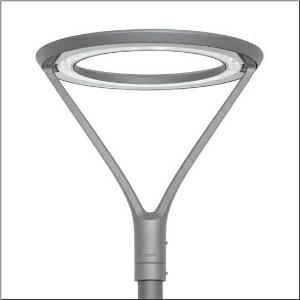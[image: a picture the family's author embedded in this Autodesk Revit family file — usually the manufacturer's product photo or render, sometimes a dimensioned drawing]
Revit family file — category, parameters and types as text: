
# Revit family: dl_r__20___pl1_2s_5xa51283ns008p_0781
name_source: partatom
category: Lighting Fixtures
units: mm (PartAtom-declared; Revit-internal decimal feet)

## family parameters
Cut with Voids When Loaded = No
Host = Face
Light Source = No
Part Type = Normal
Room Calculation Point = No
Round Connector Dimension = Use Diameter
Shared = No

## types (1)
- --- (1 x LED, 5400 lm, 41.9 W, 4000K)
    Apparent Load = 42 VA
    CIE Flux Codes = 33 78 99 100 100
    Color Rendering = 70
    Color Temperature = 4000K
    Default Elevation = 1800 mm
    Description = DL® 20, mast luminaire, primary light control with reflector, highly specular, primary optical cover: cover, of toughened safety glass of clear glass with excellent transmission level, light distribution: PL1.2s, light emission: direct distribution, primary light characteristic: symmetric, installation type: post-top, LED, High Power LED, rated luminous flux: 5.340lm, luminous efficacy: 101lm/W, light colour: 740, colour temperature: 4000K, control gear: Plus, control: overheat protection, power reduction, digital communication interface, constant luminous flux control, time-dependent luminous flux control, flexible luminous flux parameterisation, electronic power reduction, mains connection: 230..240V, 50/60Hz, connection cable pre-assembled, cable length: 5m, start of lifetime: 53W, end of service life: 54W, reduction: 24W, luminaire housing, upper part, of cast aluminium, powder-coated, Siteco® metallic grey (DB 702S), diameter: 690mm, height: 690mm, spigot size: 76mm (post-top), mounting height: 4..6m, luminaire housing, of cast aluminium, powder-coated, Siteco® metallic grey (DB 702S), equipment: Power, protection rating (complete): IP66, insulation class (complete): insulation class II (safety insulation), certification: CE, ENEC, VDE, impact resistance: IK08, permissible operating ambient temperature: -25..+30°C, standard-compliant lighting for roads and squares, packaging unit: 1 piece

Light Distribution: PL1.2s
    Height = 690 mm
    Lamp = 1 x LED
    Lamp Light Flux = 5400 lm
    Lamp Power = 41.9 W
    Lamp count = 1
    Length = 690 mm
    Luminous efficacy = 129 lm/W
    Manufacturer = Siteco
    ModVariant = No
    Model = 5XA51283NS008P
    Number of Poles = 1
    OnlyDefault = Yes
    Power Factor = 1
    Product Name = DL® 20 | PL1.2s
    Product group = mast luminaire | pylon top
    ProductGroupID = 6100
    Protection Class = Protection class II
    Protection Degree = IP 66
    RLX_Detail_Level = 1
    RLX_Emergency_Light_Flux = 0 lm
    RLX_Emergency_Type = 0
    RLX_Emergency_Type_DB = No
    RlxData = <blob elided: 204513 chars, md5=36736855>
    Socket = socket
    Standby Power = 0 W
    System Light Flux = 5400 lm
    System Power = 42 W
    Type Comments = factory setting: luminous flux: 100 % | dim-lin: 254 | 565 mA
    Type Image = l_1006001.jpg
    URL = http://relux.com
    VarID = @adj_098381
    Voltage = 0 V
    Weight = 0.00 kg
    Width = 0 mm  [stored 0 ft]

note: [stored X ft] marks values corroborated as IEEE doubles in the binary element streams (Revit-internal decimal feet)

## geometry (parser evidence)
native form markers: Blend x4, Sweep x11
no freeform markers — native parametric forms only
